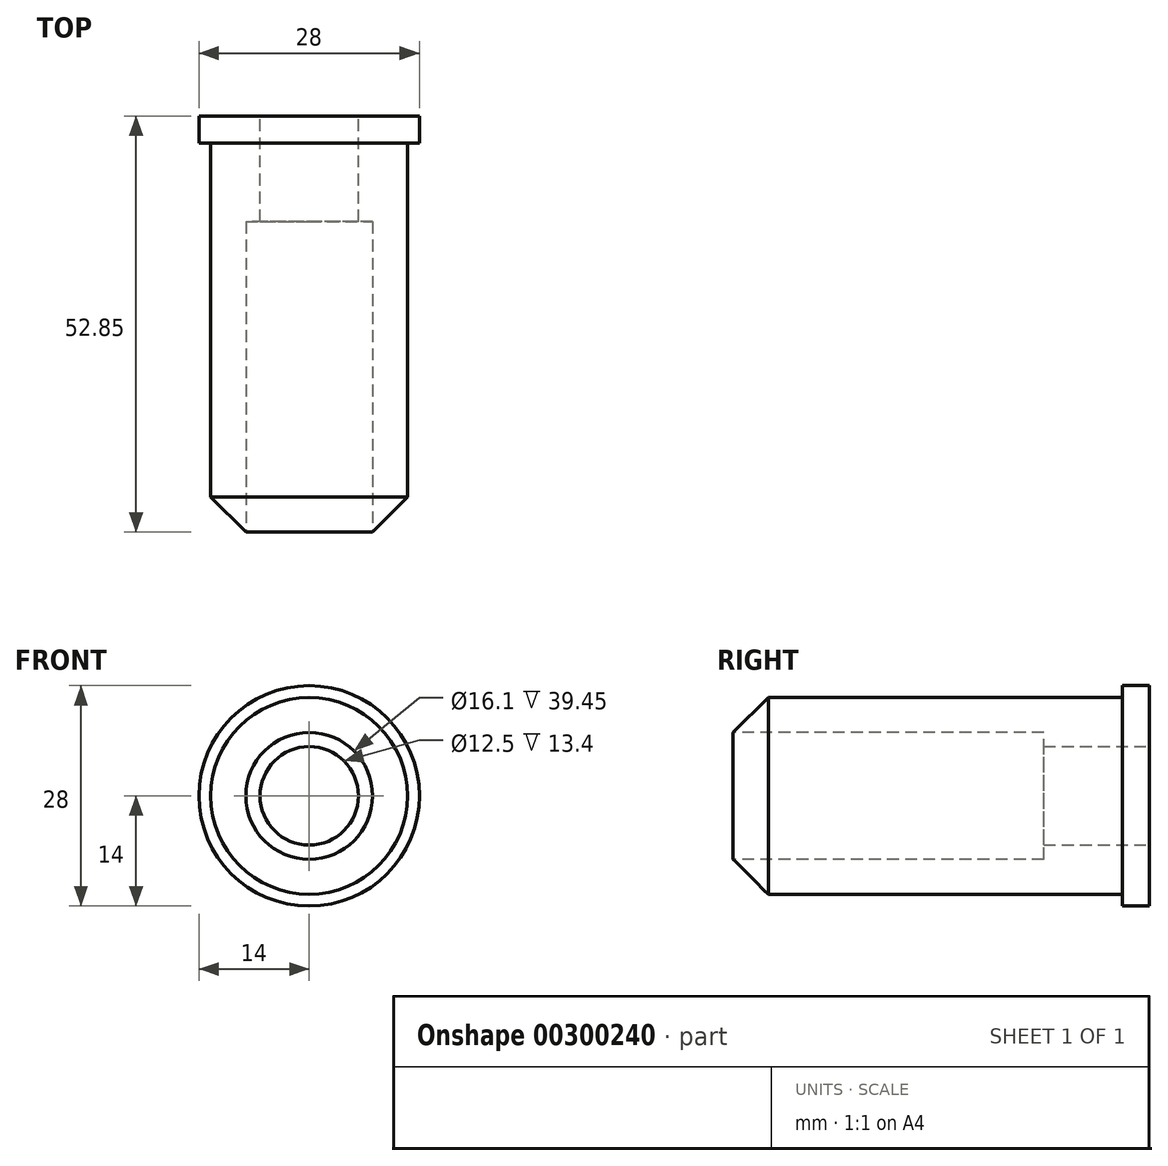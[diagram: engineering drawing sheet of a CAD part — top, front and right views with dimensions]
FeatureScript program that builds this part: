
annotation { "Feature Type Name" : "Feature", "Feature Type Description" : "" }
export const myFeature = defineFeature(function(context is Context, id is Id, definition is map)
    precondition{}
    {
        {
            var Q0;
            Q0=qCreatedBy(makeId("Front.planeOp"),FACE);
            var sketch = newSketch(context, id + "F0", { "sketchPlane" : qUnion([Q0])});
            skCircle(sketch, "E0", {"center": v(0, 0) * mm, "radius": 14 * mm});
            skSolve(sketch);
        }
        {
            var Q0;
            Q0 = qSketchRegion(id + "F0", true);
            extrude(context, id + "F1", {"entities" : qUnion([Q0]), "depth" : 3.4 * mm});
        }
        {
            var Q0;
            Q0=makeQuery(id+"F1.opExtrude","CAP_FACE",FACE,{"disambiguationData":[OSD([sQuery(id+"F0.wireOp",EDGE,"E0")])],"isStart":false});
            cPlane(context, id + "F2", {"entities" : qUnion([Q0]), "cplaneType" : CPlaneType.OFFSET, "offset" : 0 * mm, "width" : 150 * mm, "height" : 150 * mm});
        }
        {
            var Q0;
            Q0=qCreatedBy(id+"F2.planeOp",FACE);
            var sketch = newSketch(context, id + "F3", { "sketchPlane" : qUnion([Q0])});
            skCircle(sketch, "E1", {"center": v(0, 0) * mm, "radius": 12.5 * mm});
            skSolve(sketch);
        }
        {
            var Q0;
            Q0 = qSketchRegion(id + "F3", true);
            extrude(context, id + "F4", {"entities" : qUnion([Q0]), "operationType" : NewBodyOperationType.ADD, "depth" : 50 * mm});
        }
        {
            var Q0;
            Q0=makeQuery(id+"F4.opExtrude","CAP_FACE",FACE,{"disambiguationData":[OSD([sQuery(id+"F3.wireOp",EDGE,"E1")])],"isStart":false});
            cPlane(context, id + "F5", {"entities" : qUnion([Q0]), "cplaneType" : CPlaneType.OFFSET, "offset" : 0 * mm, "width" : 150 * mm, "height" : 150 * mm});
        }
        {
            var Q0;
            Q0=qCreatedBy(id+"F5.planeOp",FACE);
            var sketch = newSketch(context, id + "F6", { "sketchPlane" : qUnion([Q0])});
            skCircle(sketch, "E2", {"center": v(0, 0) * mm, "radius": 8.05 * mm});
            skSolve(sketch);
        }
        {
            var Q0;
            Q0 = qSketchRegion(id + "F6", true);
            extrude(context, id + "F7", {"entities" : qUnion([Q0]), "operationType" : NewBodyOperationType.REMOVE, "oppositeDirection" : true, "depth" : 40 * mm});
        }
        {
            var Q0;
            Q0=makeQuery(id+"F4.opExtrude","CAP_EDGE",EDGE,{"disambiguationData":[OSD([sQuery(id+"F3.wireOp",EDGE,"E1")])],"isStart":false});
            chamfer(context, id + "F8", {"entities" : qUnion([Q0]), "width" : 5 * mm, "tangentPropagation" : true});
        }
        {
            var Q0;
            Q0=qCreatedBy(makeId("Front.planeOp"),FACE);
            var sketch = newSketch(context, id + "F9", { "sketchPlane" : qUnion([Q0])});
            skCircle(sketch, "E3", {"center": v(0, 0) * mm, "radius": 6.25 * mm});
            skSolve(sketch);
        }
        {
            var Q0;
            Q0 = qSketchRegion(id + "F9", true);
            extrude(context, id + "F10", {"entities" : qUnion([Q0]), "operationType" : NewBodyOperationType.REMOVE, "depth" : 66.1 * mm});
        }
        {
            var Q0;
            Q0=makeQuery(id+"F1.opExtrude","CAP_FACE",FACE,{"disambiguationData":[OSD([sQuery(id+"F0.wireOp",EDGE,"E0")])],"isStart":true});
            cPlane(context, id + "F11", {"entities" : qUnion([Q0]), "cplaneType" : CPlaneType.OFFSET, "offset" : 0 * mm, "width" : 150 * mm, "height" : 150 * mm});
        }
    });
